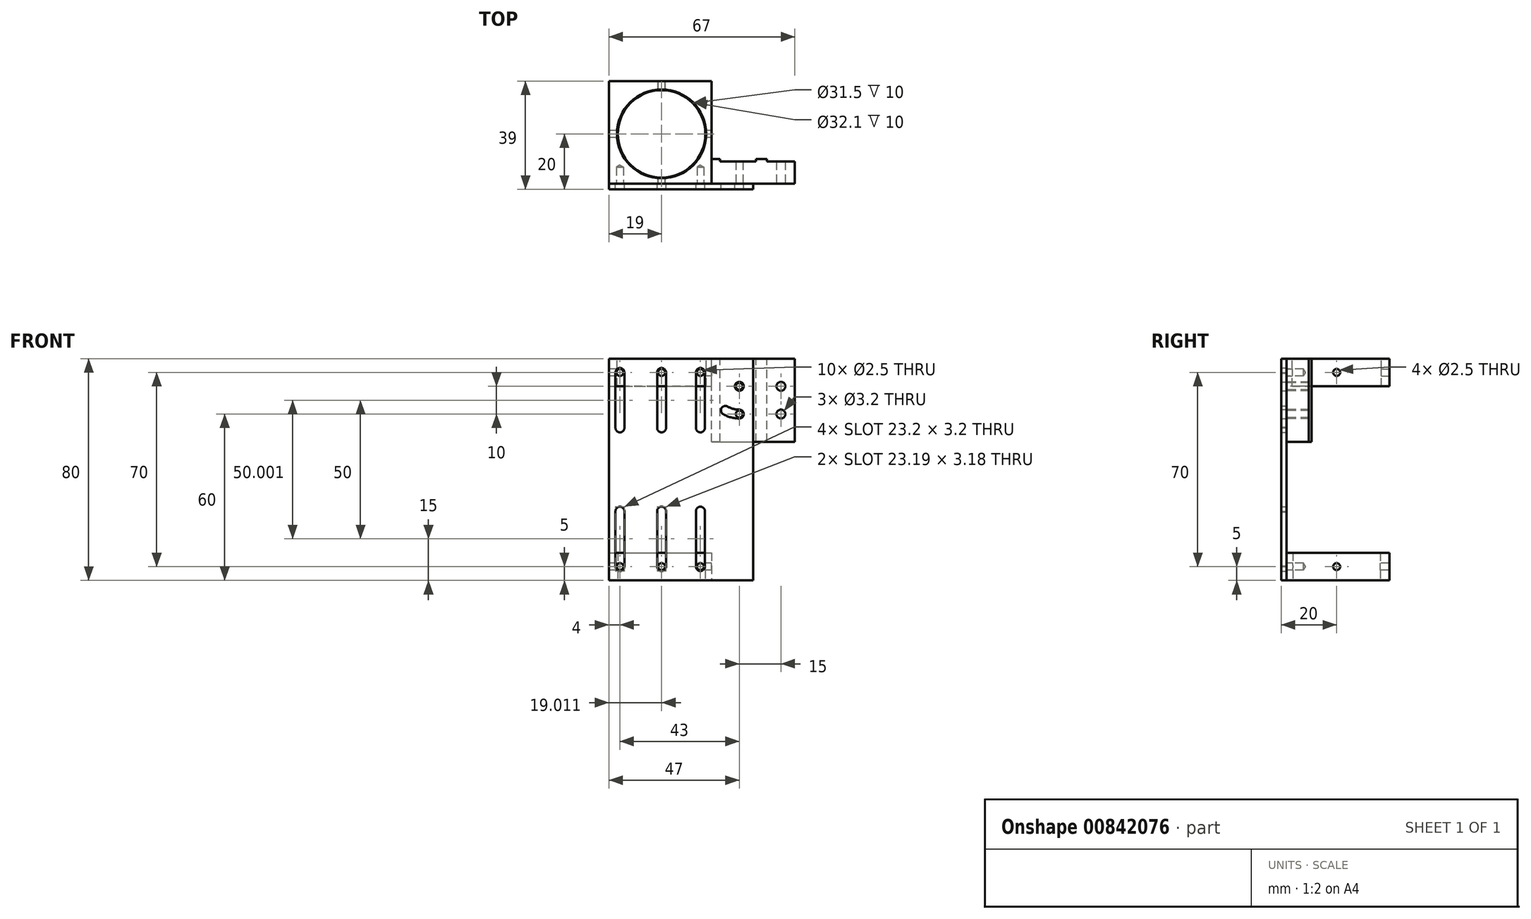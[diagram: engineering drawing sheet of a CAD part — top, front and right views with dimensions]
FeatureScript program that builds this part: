
annotation { "Feature Type Name" : "Feature", "Feature Type Description" : "" }
export const myFeature = defineFeature(function(context is Context, id is Id, definition is map)
    precondition{}
    {
        {
            var Q0;
            Q0=qCreatedBy(makeId("Top.planeOp"),FACE);
            var sketch = newSketch(context, id + "F0", { "sketchPlane" : qUnion([Q0])});
            skCircle(sketch, "E0", {"center": v(0, 0) * mm, "radius": 16.05 * mm, "construction": true});
            skLineSegment(sketch, "E1.bottom", {"start": v(21, -10) * mm, "end": v(34, -10) * mm});
            skLineSegment(sketch, "E1.top", {"start": v(18, -18) * mm, "end": v(48, -18) * mm});
            skLineSegment(sketch, "E1.left", {"start": v(18, -10) * mm, "end": v(18, -18) * mm});
            skLineSegment(sketch, "E1.right", {"start": v(48, -10) * mm, "end": v(48, -18) * mm});
            skLineSegment(sketch, "E2.top", {"start": v(34, -9) * mm, "end": v(38, -9) * mm});
            skLineSegment(sketch, "E2.left", {"start": v(34, -10) * mm, "end": v(34, -9) * mm});
            skLineSegment(sketch, "E2.right", {"start": v(38, -10) * mm, "end": v(38, -9) * mm});
            skLineSegment(sketch, "E3.bottom", {"start": v(21, -9) * mm, "end": v(18, -9) * mm});
            skLineSegment(sketch, "E3.left", {"start": v(21, -9) * mm, "end": v(21, -10) * mm});
            skLineSegment(sketch, "E3.right", {"start": v(18, -9) * mm, "end": v(18, -10) * mm});
            skLineSegment(sketch, "E4.trimOffspring", {"start": v(38, -10) * mm, "end": v(48, -10) * mm});
            skSolve(sketch);
        }
        {
            var Q0;
            Q0 = qSketchRegion(id + "F0", true);
            extrude(context, id + "F1", {"entities" : qUnion([Q0]), "oppositeDirection" : true, "depth" : 30 * mm, "offsetDistance" : 25 * mm});
        }
        {
            var Q0;
            Q0=makeQuery(id+"F1.opExtrude","SWEPT_FACE",FACE,{"disambiguationData":[OSD([sQuery(id+"F0.wireOp",EDGE,"E1.top")])]});
            var sketch = newSketch(context, id + "F2", { "sketchPlane" : qUnion([Q0])});
            skCircle(sketch, "E5", {"center": v(43, -10) * mm, "radius": 1.6 * mm});
            skCircle(sketch, "E6", {"center": v(43, -20) * mm, "radius": 1.6 * mm});
            skPoint(sketch, "E7", {"position": v(28, -10) * mm});
            skPoint(sketch, "E8", {"position": v(28, -20) * mm});
            skSolve(sketch);
        }
        {
            var Q0;
            Q0 = qSketchRegion(id + "F2", true);
            extrude(context, id + "F3", {"entities" : qUnion([Q0]), "operationType" : NewBodyOperationType.REMOVE, "oppositeDirection" : true, "depth" : 25 * mm, "offsetDistance" : 25 * mm});
        }
        {
            var Q0;
            Q0=sQuery(id+"F2.wireOp",VERTEX,"E7");
            var Q1;
            Q1=sQuery(id+"F2.wireOp",VERTEX,"E8");
            var Q2;
            Q2=makeQuery(id+"F1.opExtrude","SWEPT_BODY",BODY,{"disambiguationData":[OSD([sQuery(id+"F0.wireOp",EDGE,"E1.bottom"),sQuery(id+"F0.wireOp",EDGE,"E1.top"),sQuery(id+"F0.wireOp",EDGE,"E1.left"),sQuery(id+"F0.wireOp",EDGE,"E1.right"),sQuery(id+"F0.wireOp",EDGE,"E2.top"),sQuery(id+"F0.wireOp",EDGE,"E2.left"),sQuery(id+"F0.wireOp",EDGE,"E2.right"),sQuery(id+"F0.wireOp",EDGE,"E3.bottom"),sQuery(id+"F0.wireOp",EDGE,"E3.left"),sQuery(id+"F0.wireOp",EDGE,"E3.right"),sQuery(id+"F0.wireOp",EDGE,"E4.trimOffspring")])]});
            hole(context, id + "F4", {"style" : HoleStyle.SIMPLE, "endStyle" : HoleEndStyle.THROUGH, "standardTappedOrClearance" : lookupTablePath({ "standard" : "ISO", "engagement" : "75%", "pitch" : "0.5 mm", "size" : "M3", "type" : "Tapped" }), "standardBlindInLast" : lookupTablePath({ "standard" : "ISO", "engagement" : "75%", "pitch" : "0.5 mm", "size" : "M3", "type" : "Tapped" }), "holeDiameter" : 2.5 * mm, "majorDiameter" : 3 * mm, "showTappedDepth" : true, "isTappedThrough" : true, "tappedDepth" : 4.5 * mm, "tapClearance" : 3, "startFromSketch" : true, "locations" : qUnion([Q0, Q1]), "scope" : qUnion([Q2])});
        }
        {
            var Q0;
            Q0=qCreatedBy(makeId("Top.planeOp"),FACE);
            var sketch = newSketch(context, id + "F5", { "sketchPlane" : qUnion([Q0])});
            skCircle(sketch, "E9", {"center": v(0, 0) * mm, "radius": 16.05 * mm});
            skLineSegment(sketch, "E10.bottom", {"start": v(-19, 19) * mm, "end": v(18, 19) * mm});
            skLineSegment(sketch, "E10.top", {"start": v(-19, -18) * mm, "end": v(18, -18) * mm});
            skLineSegment(sketch, "E10.left", {"start": v(-19, 19) * mm, "end": v(-19, -18) * mm});
            skLineSegment(sketch, "E10.right", {"start": v(18, 19) * mm, "end": v(18, -18) * mm});
            skSolve(sketch);
        }
        {
            var Q0;
            Q0 = qSketchRegion(id + "F5", true);
            extrude(context, id + "F6", {"entities" : qUnion([Q0]), "oppositeDirection" : true, "depth" : 10 * mm, "offsetDistance" : 25 * mm});
        }
        {
            var Q0;
            Q0=makeQuery(id+"F6.opExtrude","SWEPT_FACE",FACE,{"disambiguationData":[OSD([sQuery(id+"F5.wireOp",EDGE,"E10.left")])]});
            var sketch = newSketch(context, id + "F7", { "sketchPlane" : qUnion([Q0])});
            skPoint(sketch, "E11", {"position": v(0, -5) * mm});
            skSolve(sketch);
        }
        {
            var Q0;
            Q0=makeQuery(id+"F6.opExtrude","SWEPT_FACE",FACE,{"disambiguationData":[OSD([sQuery(id+"F5.wireOp",EDGE,"E10.bottom")])]});
            var sketch = newSketch(context, id + "F8", { "sketchPlane" : qUnion([Q0])});
            skPoint(sketch, "E12", {"position": v(0, -5) * mm});
            skPoint(sketch, "E12.positionSnap0", {"position": v(-18, -5) * mm});
            skSolve(sketch);
        }
        {
            var Q0;
            Q0=sQuery(id+"F8.wireOp",VERTEX,"E12");
            var Q1;
            Q1=sQuery(id+"F7.wireOp",VERTEX,"E11");
            var Q2;
            Q2=makeQuery(id+"F6.opExtrude","SWEPT_BODY",BODY,{"disambiguationData":[OSD([sQuery(id+"F5.wireOp",EDGE,"E9"),sQuery(id+"F5.wireOp",EDGE,"E10.bottom"),sQuery(id+"F5.wireOp",EDGE,"E10.top"),sQuery(id+"F5.wireOp",EDGE,"E10.left"),sQuery(id+"F5.wireOp",EDGE,"E10.right")])]});
            hole(context, id + "F9", {"style" : HoleStyle.SIMPLE, "endStyle" : HoleEndStyle.THROUGH, "standardTappedOrClearance" : lookupTablePath({ "standard" : "ISO", "engagement" : "75%", "pitch" : "0.5 mm", "size" : "M3", "type" : "Tapped" }), "standardBlindInLast" : lookupTablePath({ "standard" : "ISO", "engagement" : "75%", "pitch" : "0.5 mm", "size" : "M3", "type" : "Tapped" }), "holeDiameter" : 2.5 * mm, "majorDiameter" : 3 * mm, "showTappedDepth" : true, "tappedDepth" : 4.5 * mm, "tapClearance" : 3, "startFromSketch" : true, "locations" : qUnion([Q0, Q1]), "scope" : qUnion([Q2])});
        }
        {
            var Q0;
            Q0=makeQuery(id+"F6.opExtrude","SWEPT_FACE",FACE,{"disambiguationData":[OSD([sQuery(id+"F5.wireOp",EDGE,"E10.top")])]});
            var sketch = newSketch(context, id + "F10", { "sketchPlane" : qUnion([Q0])});
            skPoint(sketch, "E13", {"position": v(-15, -5) * mm});
            skPoint(sketch, "E13.positionSnap0", {"position": v(-19, -5) * mm});
            skPoint(sketch, "E14", {"position": v(14, -5) * mm});
            skPoint(sketch, "E14.positionSnap0", {"position": v(18, -5) * mm});
            skSolve(sketch);
        }
        {
            var Q0;
            Q0=sQuery(id+"F10.wireOp",VERTEX,"E13");
            var Q1;
            Q1=sQuery(id+"F10.wireOp",VERTEX,"E14");
            var Q2;
            Q2=makeQuery(id+"F6.opExtrude","SWEPT_BODY",BODY,{"disambiguationData":[OSD([sQuery(id+"F5.wireOp",EDGE,"E9"),sQuery(id+"F5.wireOp",EDGE,"E10.bottom"),sQuery(id+"F5.wireOp",EDGE,"E10.top"),sQuery(id+"F5.wireOp",EDGE,"E10.left"),sQuery(id+"F5.wireOp",EDGE,"E10.right")])]});
            hole(context, id + "F11", {"style" : HoleStyle.SIMPLE, "endStyle" : HoleEndStyle.BLIND, "standardTappedOrClearance" : lookupTablePath({ "standard" : "ISO", "engagement" : "75%", "pitch" : "0.5 mm", "size" : "M3", "type" : "Tapped" }), "standardBlindInLast" : lookupTablePath({ "standard" : "ISO", "engagement" : "75%", "pitch" : "0.5 mm", "size" : "M3", "type" : "Tapped" }), "holeDiameter" : 2.5 * mm, "majorDiameter" : 3 * mm, "showTappedDepth" : true, "holeDepth" : 6 * mm, "tappedDepth" : 4.5 * mm, "tapClearance" : 3, "startFromSketch" : true, "locations" : qUnion([Q0, Q1]), "scope" : qUnion([Q2])});
        }
        {
            var Q0;
            Q0=makeQuery(id+"F2.imprint","IMPRINT",FACE,{"disambiguationData":[TD([[makeQuery(id+"F2.imprint","IMPRINT",EDGE,{"derivedFrom":sQuery(id+"F2.wireOp",EDGE,"E5")}),-1.0]])]});
            cPlane(context, id + "F12", {"entities" : qUnion([Q0]), "cplaneType" : CPlaneType.OFFSET, "offset" : 0 * mm, "width" : 150 * mm, "height" : 150 * mm});
        }
        {
            var Q0;
            Q0=qCreatedBy(id+"F12.planeOp",FACE);
            var sketch = newSketch(context, id + "F13", { "sketchPlane" : qUnion([Q0])});
            skLineSegment(sketch, "E15.bottom", {"start": v(-19, 0) * mm, "end": v(33, 0) * mm});
            skLineSegment(sketch, "E15.top", {"start": v(-19, -80) * mm, "end": v(33, -80) * mm});
            skLineSegment(sketch, "E15.left", {"start": v(-19, 0) * mm, "end": v(-19, -80) * mm});
            skLineSegment(sketch, "E15.right", {"start": v(33, 0) * mm, "end": v(33, -80) * mm});
            skLineSegment(sketch, "E16.left", {"start": v(33, 0) * mm, "end": v(33, -30) * mm});
            skArc(sketch, "E17", {"start": v(-13.4, -5.05) * mm, "mid": v(-14.97, -3.4) * mm, "end": v(-16.6, -5) * mm});
            skArc(sketch, "E18", {"start": v(15.59, -5.2) * mm, "mid": v(14.08, -3.4) * mm, "end": v(12.4, -5.03) * mm});
            skCircle(sketch, "E19", {"center": v(28, -10) * mm, "radius": 1.6 * mm});
            skArc(sketch, "E20", {"start": v(1.6, -5.02) * mm, "mid": v(-0.12, -3.4) * mm, "end": v(-1.58, -5.26) * mm});
            skLineSegment(sketch, "E21", {"start": v(-19, -15) * mm, "end": v(33, -15) * mm, "construction": true});
            skArc(sketch, "E22.MirrorC", {"start": v(-13.4, -25) * mm, "mid": v(-15, -26.6) * mm, "end": v(-16.6, -25) * mm});
            skArc(sketch, "E23.MirrorC", {"start": v(1.6, -25) * mm, "mid": v(-0.13, -26.6) * mm, "end": v(-1.58, -24.74) * mm});
            skArc(sketch, "E24.MirrorC", {"start": v(15.6, -25) * mm, "mid": v(13.99, -26.6) * mm, "end": v(12.4, -24.97) * mm});
            skLineSegment(sketch, "E25", {"start": v(-19, -40) * mm, "end": v(33, -40) * mm, "construction": true});
            skLineSegment(sketch, "E26", {"start": v(-16.6, -5) * mm, "end": v(-16.6, -25) * mm});
            skLineSegment(sketch, "E27", {"start": v(-13.4, -5.05) * mm, "end": v(-13.4, -25) * mm});
            skLineSegment(sketch, "E28", {"start": v(-1.58, -5.26) * mm, "end": v(-1.58, -24.74) * mm});
            skLineSegment(sketch, "E29", {"start": v(1.6, -5.02) * mm, "end": v(1.6, -25) * mm});
            skLineSegment(sketch, "E30", {"start": v(12.4, -4.97) * mm, "end": v(12.4, -24.97) * mm});
            skLineSegment(sketch, "E31", {"start": v(15.59, -4.8) * mm, "end": v(15.6, -25) * mm});
            skLineSegment(sketch, "E32.MirrorCS", {"start": v(-16.6, -75) * mm, "end": v(-16.6, -55) * mm});
            skArc(sketch, "E33.MirrorCS", {"start": v(-13.4, -74.95) * mm, "mid": v(-14.97, -76.6) * mm, "end": v(-16.6, -75) * mm});
            skLineSegment(sketch, "E34.MirrorCS", {"start": v(-13.4, -74.95) * mm, "end": v(-13.4, -55) * mm});
            skArc(sketch, "E35.MirrorCS", {"start": v(-13.4, -55) * mm, "mid": v(-15, -53.4) * mm, "end": v(-16.6, -55) * mm});
            skArc(sketch, "E36.MirrorCS", {"start": v(1.6, -74.98) * mm, "mid": v(-0.12, -76.6) * mm, "end": v(-1.58, -74.74) * mm});
            skLineSegment(sketch, "E37.MirrorCS", {"start": v(-1.58, -74.74) * mm, "end": v(-1.58, -55.26) * mm});
            skLineSegment(sketch, "E38.MirrorCS", {"start": v(1.6, -74.98) * mm, "end": v(1.6, -55) * mm});
            skArc(sketch, "E39.MirrorCS", {"start": v(1.6, -55) * mm, "mid": v(-0.13, -53.4) * mm, "end": v(-1.58, -55.26) * mm});
            skLineSegment(sketch, "E40.MirrorCS", {"start": v(12.4, -75.03) * mm, "end": v(12.4, -55.03) * mm});
            skLineSegment(sketch, "E41.MirrorCS", {"start": v(15.59, -75.2) * mm, "end": v(15.6, -55) * mm});
            skArc(sketch, "E42.MirrorCS", {"start": v(15.59, -74.8) * mm, "mid": v(14.08, -76.6) * mm, "end": v(12.4, -74.97) * mm});
            skArc(sketch, "E43.MirrorCS", {"start": v(15.6, -55) * mm, "mid": v(13.99, -53.4) * mm, "end": v(12.4, -55.03) * mm});
            skArc(sketch, "E44", {"start": v(28, -21.6) * mm, "mid": v(29.6, -20) * mm, "end": v(28, -18.4) * mm});
            skLineSegment(sketch, "E45", {"start": v(28, -10) * mm, "end": v(23, -18.66) * mm, "construction": true});
            skLineSegment(sketch, "E46", {"start": v(22.2, -20.05) * mm, "end": v(28, -10) * mm, "construction": true});
            skLineSegment(sketch, "E47", {"start": v(28, -21.6) * mm, "end": v(28, -10) * mm, "construction": true});
            skArc(sketch, "E48", {"start": v(23.8, -17.27) * mm, "mid": v(21.61, -17.86) * mm, "end": v(22.2, -20.05) * mm});
            skArc(sketch, "E49", {"start": v(28, -21.6) * mm, "mid": v(25, -21.2) * mm, "end": v(22.2, -20.05) * mm});
            skPoint(sketch, "E49.startSnap0", {"position": v(28, -15) * mm});
            skArc(sketch, "E50", {"start": v(28, -18.4) * mm, "mid": v(25.83, -18.11) * mm, "end": v(23.8, -17.27) * mm});
            skSolve(sketch);
        }
        {
            var Q0;
            Q0=makeQuery(id+"F13.imprint","IMPRINT",FACE,{"disambiguationData":[TD([[makeQuery(id+"F13.imprint","IMPRINT",EDGE,{"derivedFrom":sQuery(id+"F13.wireOp",EDGE,"E15.bottom")}),-1.0]])]});
            extrude(context, id + "F14", {"entities" : qUnion([Q0]), "depth" : 2 * mm, "offsetDistance" : 25 * mm});
        }
        {
            var Q0;
            Q0=makeQuery(id+"F14.opExtrude","SWEPT_FACE",FACE,{"disambiguationData":[OSD([sQuery(id+"F13.wireOp",EDGE,"E15.top")])]});
            cPlane(context, id + "F15", {"entities" : qUnion([Q0]), "cplaneType" : CPlaneType.OFFSET, "offset" : 0 * mm, "width" : 150 * mm, "height" : 150 * mm});
        }
        {
            var Q0;
            Q0=qCreatedBy(id+"F15.planeOp",FACE);
            var sketch = newSketch(context, id + "F16", { "sketchPlane" : qUnion([Q0])});
            skCircle(sketch, "E51", {"center": v(0, 0) * mm, "radius": 15.75 * mm});
            skLineSegment(sketch, "E52.bottom", {"start": v(-19, -19) * mm, "end": v(18, -19) * mm});
            skLineSegment(sketch, "E52.top", {"start": v(-19, 18) * mm, "end": v(18, 18) * mm});
            skLineSegment(sketch, "E52.left", {"start": v(-19, -19) * mm, "end": v(-19, 18) * mm});
            skLineSegment(sketch, "E52.right", {"start": v(18, -19) * mm, "end": v(18, 18) * mm});
            skSolve(sketch);
        }
        {
            var Q0;
            Q0=makeQuery(id+"F16.imprint","IMPRINT",FACE,{"disambiguationData":[TD([[makeQuery(id+"F16.imprint","IMPRINT",EDGE,{"derivedFrom":sQuery(id+"F16.wireOp",EDGE,"E51")}),-1.0]])]});
            extrude(context, id + "F17", {"entities" : qUnion([Q0]), "oppositeDirection" : true, "depth" : 10 * mm, "offsetDistance" : 25 * mm});
        }
        {
            var Q0;
            Q0=makeQuery(id+"F17.opExtrude","SWEPT_FACE",FACE,{"disambiguationData":[OSD([sQuery(id+"F16.wireOp",EDGE,"E52.top")])]});
            var sketch = newSketch(context, id + "F18", { "sketchPlane" : qUnion([Q0])});
            skPoint(sketch, "E53", {"position": v(-15, -75) * mm});
            skPoint(sketch, "E53.positionSnap0", {"position": v(-19, -75) * mm});
            skPoint(sketch, "E54", {"position": v(14, -75) * mm});
            skPoint(sketch, "E54.positionSnap0", {"position": v(18, -75) * mm});
            skPoint(sketch, "E55", {"position": v(0, -75) * mm});
            skSolve(sketch);
        }
        {
            var Q0;
            Q0=sQuery(id+"F18.wireOp",VERTEX,"E53");
            var Q1;
            Q1=sQuery(id+"F18.wireOp",VERTEX,"E54");
            var Q2;
            Q2=makeQuery(id+"F17.opExtrude","SWEPT_BODY",BODY,{"disambiguationData":[OSD([sQuery(id+"F16.wireOp",EDGE,"E51"),sQuery(id+"F16.wireOp",EDGE,"E52.bottom"),sQuery(id+"F16.wireOp",EDGE,"E52.top"),sQuery(id+"F16.wireOp",EDGE,"E52.left"),sQuery(id+"F16.wireOp",EDGE,"E52.right")])]});
            hole(context, id + "F19", {"style" : HoleStyle.SIMPLE, "endStyle" : HoleEndStyle.BLIND, "standardTappedOrClearance" : lookupTablePath({ "standard" : "ISO", "engagement" : "75%", "pitch" : "0.5 mm", "size" : "M3", "type" : "Tapped" }), "standardBlindInLast" : lookupTablePath({ "standard" : "ISO", "engagement" : "75%", "pitch" : "0.5 mm", "size" : "M3", "type" : "Tapped" }), "holeDiameter" : 2.5 * mm, "majorDiameter" : 3 * mm, "showTappedDepth" : true, "holeDepth" : 6 * mm, "tappedDepth" : 4.5 * mm, "tapClearance" : 3, "startFromSketch" : true, "locations" : qUnion([Q0, Q1]), "scope" : qUnion([Q2])});
        }
        {
            var Q0;
            Q0=sQuery(id+"F18.wireOp",VERTEX,"E55");
            var Q1;
            Q1=makeQuery(id+"F17.opExtrude","SWEPT_BODY",BODY,{"disambiguationData":[OSD([sQuery(id+"F16.wireOp",EDGE,"E51"),sQuery(id+"F16.wireOp",EDGE,"E52.bottom"),sQuery(id+"F16.wireOp",EDGE,"E52.top"),sQuery(id+"F16.wireOp",EDGE,"E52.left"),sQuery(id+"F16.wireOp",EDGE,"E52.right")])]});
            hole(context, id + "F20", {"style" : HoleStyle.SIMPLE, "endStyle" : HoleEndStyle.THROUGH, "standardTappedOrClearance" : lookupTablePath({ "standard" : "ISO", "engagement" : "75%", "pitch" : "0.5 mm", "size" : "M3", "type" : "Tapped" }), "standardBlindInLast" : lookupTablePath({ "standard" : "ISO", "engagement" : "75%", "pitch" : "0.5 mm", "size" : "M3", "type" : "Tapped" }), "holeDiameter" : 2.5 * mm, "majorDiameter" : 3 * mm, "showTappedDepth" : true, "tappedDepth" : 4.5 * mm, "tapClearance" : 3, "startFromSketch" : true, "locations" : qUnion([Q0]), "scope" : qUnion([Q1])});
        }
        {
            var Q0;
            Q0=makeQuery(id+"F17.opExtrude","SWEPT_FACE",FACE,{"disambiguationData":[OSD([sQuery(id+"F16.wireOp",EDGE,"E52.left")])]});
            var sketch = newSketch(context, id + "F21", { "sketchPlane" : qUnion([Q0])});
            skPoint(sketch, "E56", {"position": v(0, -75) * mm});
            skPoint(sketch, "E56.positionSnap0", {"position": v(-19, -75) * mm});
            skSolve(sketch);
        }
        {
            var Q0;
            Q0=sQuery(id+"F21.wireOp",VERTEX,"E56");
            var Q1;
            Q1=makeQuery(id+"F17.opExtrude","SWEPT_BODY",BODY,{"disambiguationData":[OSD([sQuery(id+"F16.wireOp",EDGE,"E51"),sQuery(id+"F16.wireOp",EDGE,"E52.bottom"),sQuery(id+"F16.wireOp",EDGE,"E52.top"),sQuery(id+"F16.wireOp",EDGE,"E52.left"),sQuery(id+"F16.wireOp",EDGE,"E52.right")])]});
            hole(context, id + "F22", {"style" : HoleStyle.SIMPLE, "endStyle" : HoleEndStyle.THROUGH, "standardTappedOrClearance" : lookupTablePath({ "standard" : "ISO", "engagement" : "75%", "pitch" : "0.5 mm", "size" : "M3", "type" : "Tapped" }), "standardBlindInLast" : lookupTablePath({ "standard" : "ISO", "engagement" : "75%", "pitch" : "0.5 mm", "size" : "M3", "type" : "Tapped" }), "holeDiameter" : 2.5 * mm, "majorDiameter" : 3 * mm, "showTappedDepth" : true, "tappedDepth" : 4.5 * mm, "tapClearance" : 3, "startFromSketch" : true, "locations" : qUnion([Q0]), "scope" : qUnion([Q1])});
        }
    });
